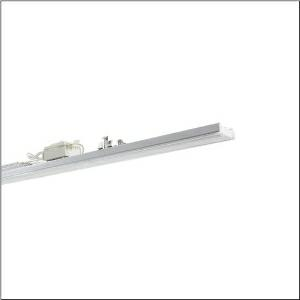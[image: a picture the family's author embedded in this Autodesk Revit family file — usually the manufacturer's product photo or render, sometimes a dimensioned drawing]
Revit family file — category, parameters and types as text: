
# Revit family: licross_r__11_recessed_ho_51tl12dn4exm3s_95e2
name_source: partatom
category: Lighting Fixtures
units: mm (PartAtom-declared; Revit-internal decimal feet)

## family parameters
Cut with Voids When Loaded = No
Host = Face
Light Source = No
Part Type = Normal
Room Calculation Point = No
Round Connector Dimension = Use Diameter
Shared = No

## types (1)
- --- (1 x LED, 1000 lm, 7.2 W, 4000K)
    Apparent Load = 7 VA
    CIE Flux Codes = 66 91 98 100 100
    Color Rendering = 80
    Color Temperature = 4000K
    Default Elevation = 1800 mm
    Description = Licross® 11 Recessed HO, luminaire insert, of sheet steel, coil coated, white, length: 1.500mm, width: 66mm, height: 67mm, LED rated luminous flux: 14.030lm, light colour: 840, control gear: DALI 2 (for two DALI lines), with plug, 6-pole, with phase selection, for trunking rail, 14-core, mains connection: 220..240V, AC, 50/60Hz, rated input power: 81W, for trunking rail, 14-core, internal wiring halogen-free, for emergency light function, converter,control gear: single battery element, battery: LiFePO4, 9Ah, primary optical cover: cover, of PMMA, light emission: direct distribution, primary light characteristic: symmetric, protection rating (complete): IP40, insulation class (complete): insulation class I (protective earthing), certification: CE, UKCA, protection symbol: D if used in an environment without relevant dust loads with corresponding accessories, impact resistance: IK06, permissible ambient temperature for indoor applications: +5..+30°C, standard: EN 60598-2-22, LABS conformity tested according to VDMA 24364:2018-05, reducing of maximum allowable ambient temperature of 5°C with ceiling mounting, corresponds to IFS (International Featured Standards) requirements for safety and quality in the food industry, packaging unit: 1 piece
    Height = 58 mm
    Lamp = 1 x LED
    Lamp Light Flux = 1000 lm
    Lamp Power = 7.2 W
    Lamp count = 1
    Length = 1500 mm
    Luminous efficacy = 139 lm/W
    Manufacturer = Siteco
    ModVariant = No
    Model = 51TL12DN4EXM3S
    Mounting Place = Ceiling
    Mounting Type = Pendant
    Number of Poles = 1
    OnlyDefault = Yes
    Power Factor = 1
    Product Name = Licross® 11 Recessed HO
    Product group = luminaire insert | ceiling pendant
    ProductGroupID = 902
    Protection Class = Protection class I
    Protection Degree = IP 40
    RLX_Detail_Level = 1
    RLX_Emergency_Light_Flux = 0 lm
    RLX_Emergency_Type = 0
    RLX_Emergency_Type_DB = No
    RlxData = <blob elided: 25001 chars, md5=a62660d4>
    Socket = socket
    Standby Power = 0 W
    System Light Flux = 1000 lm
    System Power = 7 W
    Type Comments = : emergency light operation: 3 h
    Type Image = l_1296930.jpg
    URL = http://relux.com
    VarID = @adj_111595
    Voltage = 0 V
    Weight = 0.00 kg
    Width = 66 mm

## geometry (parser evidence)
native form markers: Blend x4, Sweep x10
no freeform markers — native parametric forms only
